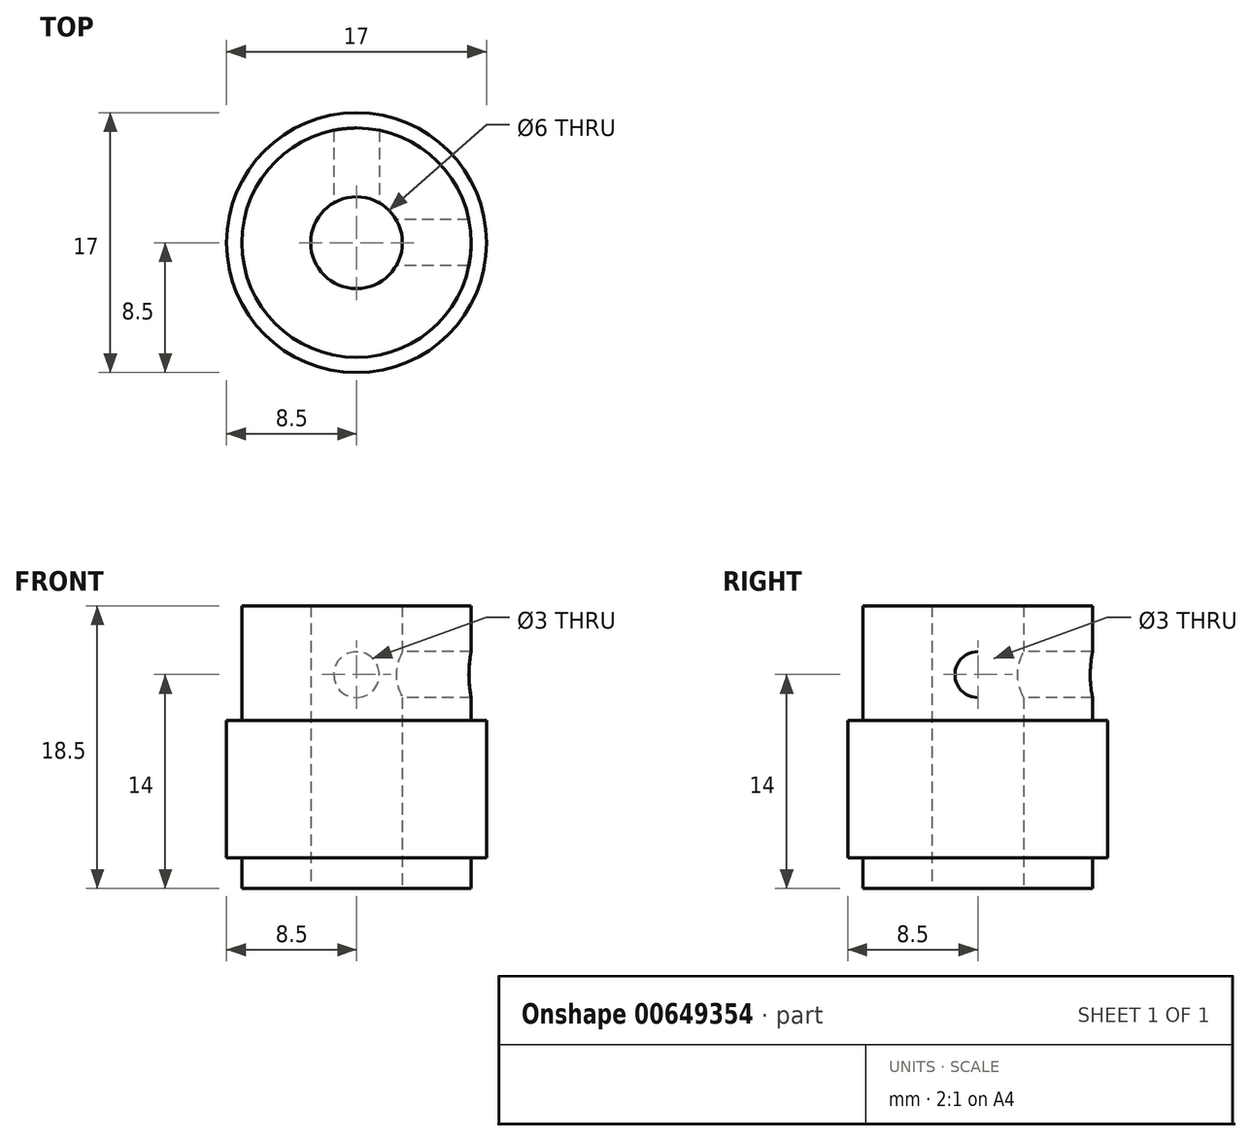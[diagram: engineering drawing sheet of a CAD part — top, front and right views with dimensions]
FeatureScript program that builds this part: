
annotation { "Feature Type Name" : "Feature", "Feature Type Description" : "" }
export const myFeature = defineFeature(function(context is Context, id is Id, definition is map)
    precondition{}
    {
        {
            var Q0;
            Q0=qCreatedBy(makeId("Top.planeOp"),FACE);
            var sketch = newSketch(context, id + "F0", { "sketchPlane" : qUnion([Q0])});
            skCircle(sketch, "E0", {"center": v(0, 0) * mm, "radius": 7.5 * mm});
            skCircle(sketch, "E1", {"center": v(0, 0) * mm, "radius": 3 * mm});
            skCircle(sketch, "E2", {"center": v(0, 0) * mm, "radius": 8.5 * mm});
            skSolve(sketch);
        }
        {
            var Q0;
            Q0=makeQuery(id+"F0.imprint","IMPRINT",FACE,{"disambiguationData":[TD([[makeQuery(id+"F0.imprint","IMPRINT",EDGE,{"derivedFrom":sQuery(id+"F0.wireOp",EDGE,"E0")}),1.0]])]});
            extrude(context, id + "F1", {"entities" : qUnion([Q0]), "depth" : 18.5 * mm, "offsetDistance" : 25 * mm});
        }
        {
            var Q0;
            Q0 = qSketchRegion(id + "F0", true);
            extrude(context, id + "F2", {"entities" : qUnion([Q0]), "operationType" : NewBodyOperationType.ADD, "depth" : 11 * mm, "offsetDistance" : 25 * mm, "hasSecondDirection" : true, "secondDirectionOppositeDirection" : false, "secondDirectionDepth" : 2 * mm});
        }
        {
            var Q0;
            Q0=qCreatedBy(makeId("Right.planeOp"),FACE);
            var sketch = newSketch(context, id + "F3", { "sketchPlane" : qUnion([Q0])});
            skCircle(sketch, "E3", {"center": v(0, 14) * mm, "radius": 1.5 * mm});
            skSolve(sketch);
        }
        {
            var Q0;
            Q0 = qSketchRegion(id + "F3", true);
            extrude(context, id + "F4", {"entities" : qUnion([Q0]), "operationType" : NewBodyOperationType.REMOVE, "endBound" : BoundingType.THROUGH_ALL, "depth" : 25 * mm, "offsetDistance" : 25 * mm});
        }
        {
            var Q0;
            Q0=qCreatedBy(makeId("Front.planeOp"),FACE);
            var sketch = newSketch(context, id + "F5", { "sketchPlane" : qUnion([Q0])});
            skCircle(sketch, "E4", {"center": v(0, 14) * mm, "radius": 1.5 * mm});
            skSolve(sketch);
        }
        {
            var Q0;
            Q0 = qSketchRegion(id + "F5", true);
            extrude(context, id + "F6", {"entities" : qUnion([Q0]), "operationType" : NewBodyOperationType.REMOVE, "endBound" : BoundingType.THROUGH_ALL, "oppositeDirection" : true, "depth" : 25 * mm, "offsetDistance" : 25 * mm});
        }
    });
